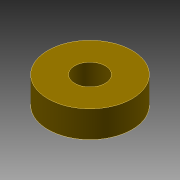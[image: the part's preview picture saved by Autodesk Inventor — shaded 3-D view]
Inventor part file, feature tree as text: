
AUTODESK INVENTOR PART (.ipt)
format: ipt  version: 2021.3 (Build 253353000, 353)  size: 95,744 bytes
history: native  units: mm
features: other x1, extrude x1, sketch x1
ambient origin geometry x8: Origin, YZ Plane, XZ Plane, XY Plane, X Axis, Y Axis, Z Axis, Center Point
bodies: Body1 (feature_tree)
feature tree (3):
  other  "Твердое тело1"
  extrude  "Выдавливание1"  Depth=8.0mm
  sketch  "Эскиз1"
